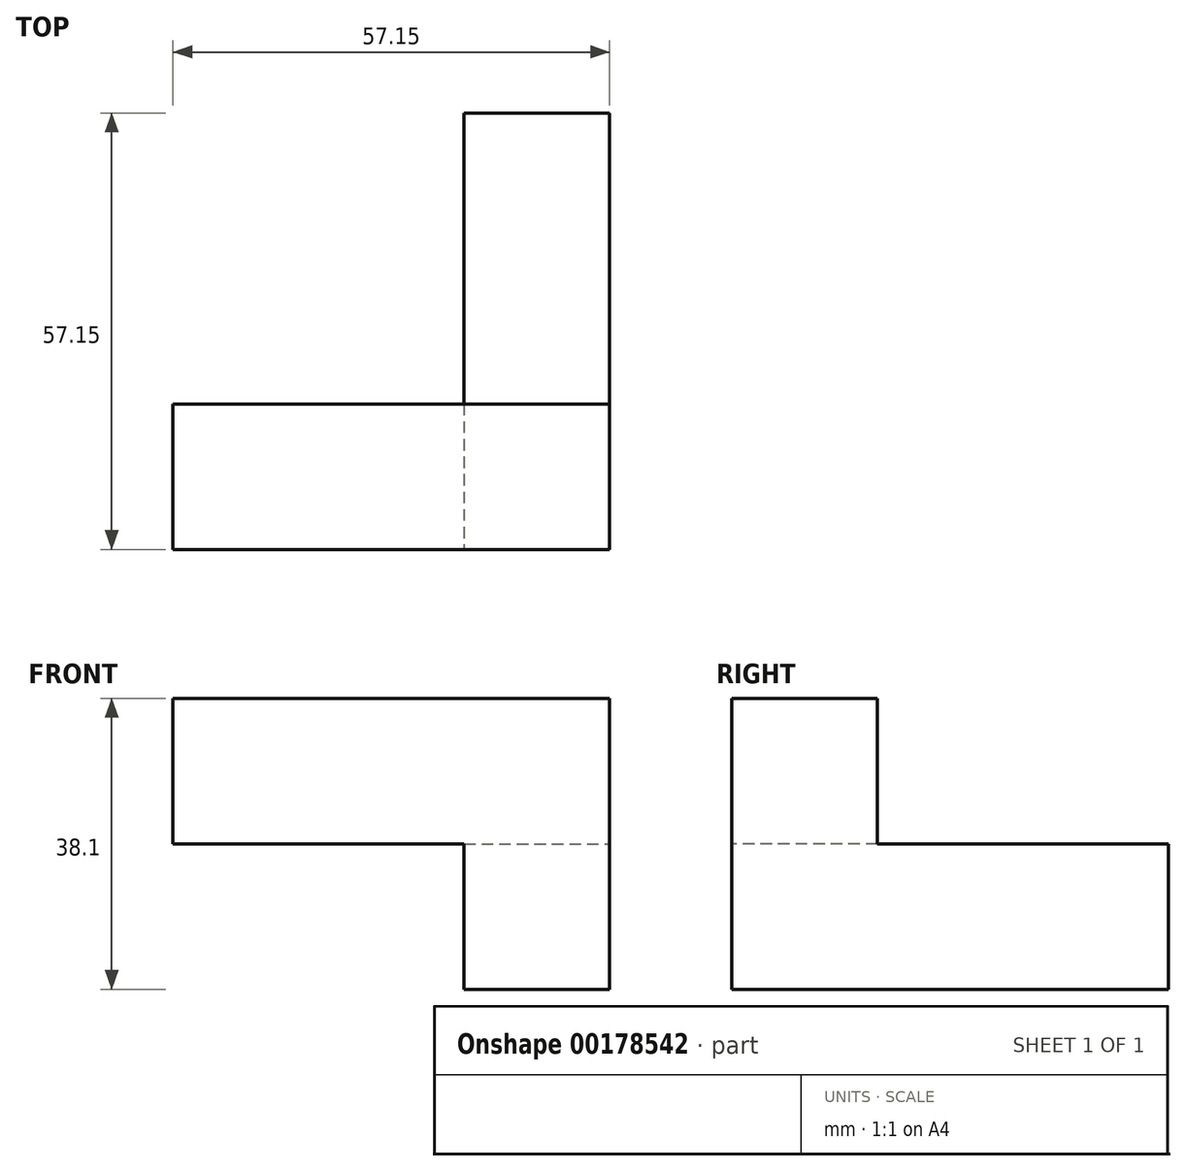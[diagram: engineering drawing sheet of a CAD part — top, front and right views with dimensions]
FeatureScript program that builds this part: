
annotation { "Feature Type Name" : "Feature", "Feature Type Description" : "" }
export const myFeature = defineFeature(function(context is Context, id is Id, definition is map)
    precondition{}
    {
        {
            var Q0;
            Q0=qCreatedBy(makeId("Front.planeOp"),FACE);
            var sketch = newSketch(context, id + "F0", { "sketchPlane" : qUnion([Q0])});
            skLineSegment(sketch, "E0.bottom", {"start": v(-79.96, 0) * mm, "end": v(-60.9, 0) * mm});
            skLineSegment(sketch, "E0.top", {"start": v(-79.96, 19.05) * mm, "end": v(-60.9, 19.05) * mm});
            skLineSegment(sketch, "E0.left", {"start": v(-79.96, 0) * mm, "end": v(-79.96, 19.05) * mm});
            skLineSegment(sketch, "E0.right", {"start": v(-60.9, 0) * mm, "end": v(-60.9, 19.05) * mm});
            skLineSegment(sketch, "E1.bottom", {"start": v(-60.9, 0) * mm, "end": v(-41.86, 0) * mm});
            skLineSegment(sketch, "E1.top", {"start": v(-60.9, 19.05) * mm, "end": v(-41.86, 19.05) * mm});
            skLineSegment(sketch, "E1.right", {"start": v(-41.86, 0) * mm, "end": v(-41.86, 19.05) * mm});
            skLineSegment(sketch, "E2.bottom", {"start": v(-41.86, 0) * mm, "end": v(-22.8, 0) * mm});
            skLineSegment(sketch, "E2.top", {"start": v(-41.86, 19.05) * mm, "end": v(-22.8, 19.05) * mm});
            skLineSegment(sketch, "E2.right", {"start": v(-22.8, 0) * mm, "end": v(-22.8, 19.05) * mm});
            skLineSegment(sketch, "E3.top", {"start": v(-41.86, -19.05) * mm, "end": v(-22.8, -19.05) * mm});
            skLineSegment(sketch, "E3.left", {"start": v(-41.86, 0) * mm, "end": v(-41.86, -19.05) * mm});
            skLineSegment(sketch, "E3.right", {"start": v(-22.8, 0) * mm, "end": v(-22.8, -19.05) * mm});
            skSolve(sketch);
        }
        {
            var Q0;
            Q0=makeQuery(id+"F0.imprint","IMPRINT",FACE,{"disambiguationData":[TD([[makeQuery(id+"F0.imprint","IMPRINT",EDGE,{"derivedFrom":sQuery(id+"F0.wireOp",EDGE,"E0.bottom")}),1.0]])]});
            extrude(context, id + "F1", {"entities" : qUnion([Q0]), "oppositeDirection" : true, "depth" : 19.05 * mm});
        }
        {
            var Q0;
            Q0=makeQuery(id+"F0.imprint","IMPRINT",FACE,{"disambiguationData":[TD([[makeQuery(id+"F0.imprint","IMPRINT",EDGE,{"derivedFrom":sQuery(id+"F0.wireOp",EDGE,"E1.bottom")}),1.0]])]});
            extrude(context, id + "F2", {"entities" : qUnion([Q0]), "operationType" : NewBodyOperationType.ADD, "oppositeDirection" : true, "depth" : 19.05 * mm});
        }
        {
            var Q0;
            Q0=makeQuery(id+"F0.imprint","IMPRINT",FACE,{"disambiguationData":[TD([[makeQuery(id+"F0.imprint","IMPRINT",EDGE,{"derivedFrom":sQuery(id+"F0.wireOp",EDGE,"E2.top")}),-1.0]])]});
            extrude(context, id + "F3", {"entities" : qUnion([Q0]), "operationType" : NewBodyOperationType.ADD, "oppositeDirection" : true, "depth" : 19.05 * mm});
        }
        {
            var Q0;
            Q0=makeQuery(id+"F0.imprint","IMPRINT",FACE,{"disambiguationData":[TD([[makeQuery(id+"F0.imprint","IMPRINT",EDGE,{"derivedFrom":sQuery(id+"F0.wireOp",EDGE,"E2.bottom")}),-1.0]])]});
            extrude(context, id + "F4", {"entities" : qUnion([Q0]), "operationType" : NewBodyOperationType.ADD, "oppositeDirection" : true, "depth" : 57.15 * mm});
        }
    });
